FCSTD DOCUMENT  (FreeCAD 1.0R38806 (Git))
Label: pinzas paralelas
License: All rights reserved
LicenseURL: https://en.wikipedia.org/wiki/All_rights_reserved
objects: Sketcher::SketchObject×1
note: 2 computed .brp shape members not serialized (recipe doc carries the construction recipe); baked Part::Feature solids carry a one-line shape summary decoded from their .brp

FEATURE [Sketcher::SketchObject] Sketch
  ArcFitTolerance = 1e-06
  FullyConstrained = false
  MakeInternals = false
  sketch-geometry (12):
    g0: LineSegment StartX=-29.9999 StartY=9.9999 StartZ=0 EndX=-20 EndY=0 EndZ=0
    g1: LineSegment StartX=-20 StartY=0 StartZ=0 EndX=0 EndY=0 EndZ=0
    g2: LineSegment StartX=-29.9999 StartY=9.9999 StartZ=0 EndX=-14.1114 EndY=22.1472 EndZ=0
    g3: LineSegment StartX=-20 StartY=0 StartZ=0 EndX=-4.11152 EndY=12.1473 EndZ=0
    g4: LineSegment StartX=-14.1114 StartY=22.1472 StartZ=0 EndX=-4.11152 EndY=12.1473 EndZ=0
    g5: LineSegment StartX=-14.1114 StartY=22.1472 StartZ=0 EndX=-14.1114 EndY=32.1472 EndZ=0
    g6: LineSegment StartX=20 StartY=0 StartZ=0 EndX=29.9999 EndY=9.9999 EndZ=0
    g7: LineSegment StartX=20 StartY=0 StartZ=0 EndX=4.11152 EndY=12.1473 EndZ=0
    g8: LineSegment StartX=29.9999 StartY=9.9999 StartZ=0 EndX=14.1114 EndY=22.1472 EndZ=0
    g9: LineSegment StartX=0 StartY=0 StartZ=0 EndX=20 EndY=0 EndZ=0
    g10: LineSegment StartX=4.11152 StartY=12.1473 StartZ=0 EndX=14.1114 EndY=22.1472 EndZ=0
    g11: LineSegment StartX=14.1114 StartY=22.1472 StartZ=0 EndX=14.1114 EndY=32.1472 EndZ=0
  constraints (32):
    c: PointOnObject(g0,g-1)
    c: Angle(g0,g-1) = 0.785398
    c: Coincident(g1,g0)
    c: Coincident(g1,g-1)
    c: DistanceX(g1,g1) = 20
    c: Distance(g0,g0) = 14.142
    c: Coincident(g2,g0)
    c: Coincident(g3,g0)
    c: Distance(g3,g3) = 20
    c: Distance(g2,g2) = 20
    c: Coincident(g4,g2)
    c: Coincident(g4,g3)
    c: Parallel(g2,g3)
    c: Distance(g5) = 10
    c: Vertical(g5)
    c: Coincident(g5,g2)
    c: Distance(g7) = 20
    c: Coincident(g7,g6)
    c: Distance(g8) = 20
    c: Coincident(g8,g6)
    c: Coincident(g9,g1)
    c: Coincident(g9,g6)
    c: Horizontal(g9)
    c: DistanceX(g9,g9) = 20
    c: Angle(g-1,g6) = 0.785398
    c: Parallel(g8,g7)
    c: Coincident(g10,g7)
    c: Coincident(g10,g8)
    c: Distance(g6,g6) = 14.142
    c: Distance(g11) = 10
    c: Coincident(g11,g8)
    c: Symmetric(g11,g5,g-2)
